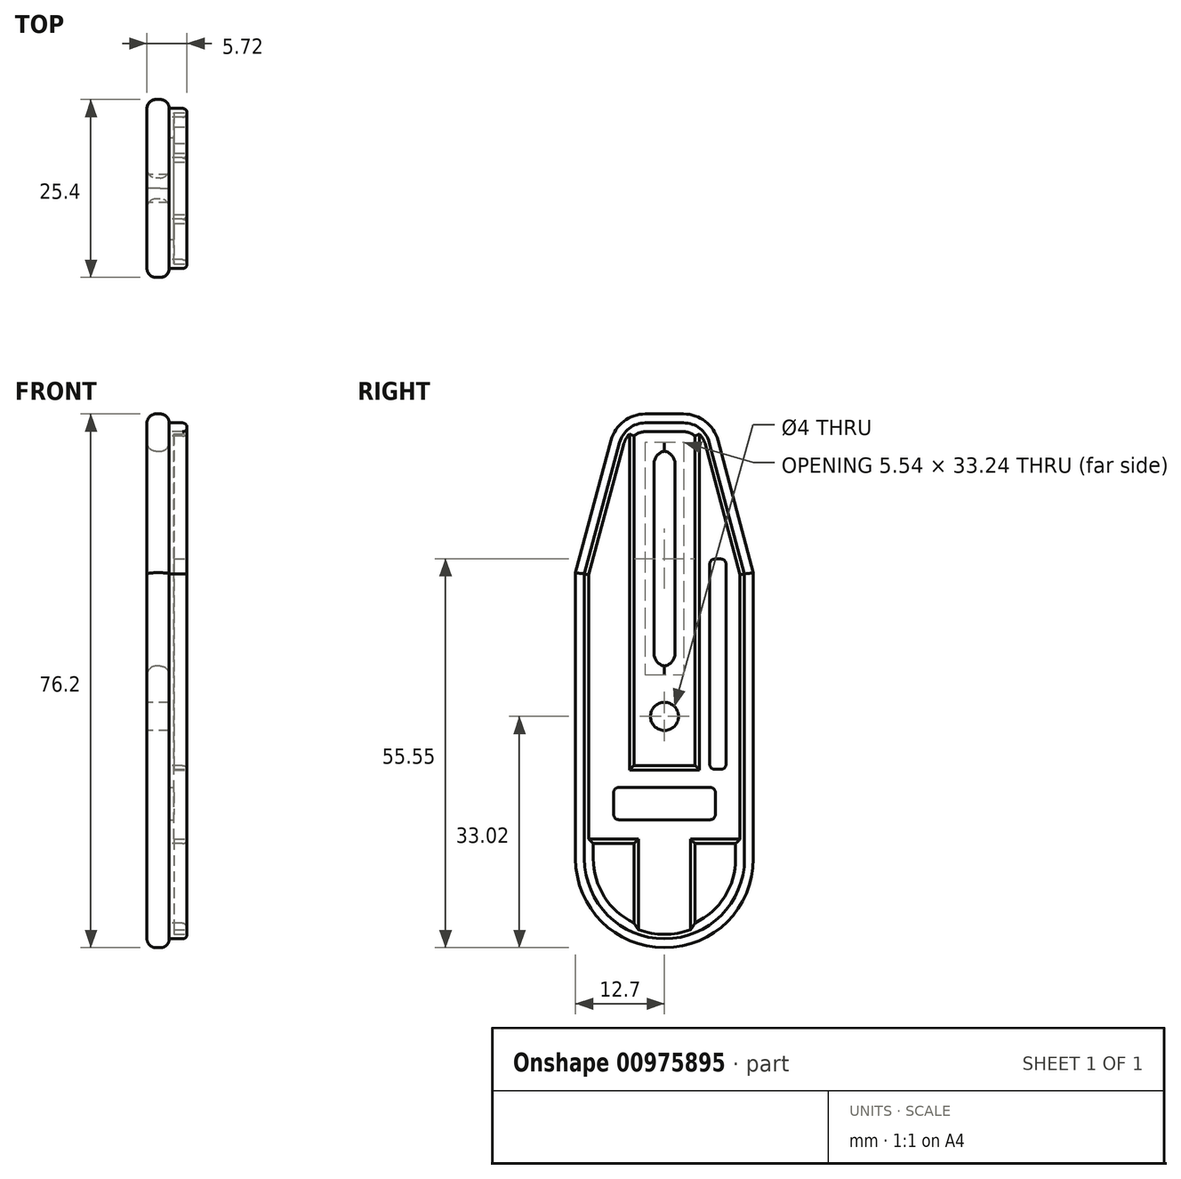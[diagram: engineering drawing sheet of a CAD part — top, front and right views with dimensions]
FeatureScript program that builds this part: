
annotation { "Feature Type Name" : "Feature", "Feature Type Description" : "" }
export const myFeature = defineFeature(function(context is Context, id is Id, definition is map)
    precondition{}
    {
        {
            var Q0;
            Q0=qCreatedBy(makeId("Right.planeOp"),FACE);
            var sketch = newSketch(context, id + "F0", { "sketchPlane" : qUnion([Q0])});
            skLineSegment(sketch, "E0", {"start": v(0, 0) * mm, "end": v(0, -40.83) * mm});
            skLineSegment(sketch, "E1", {"start": v(0, -40.83) * mm, "end": v(25.4, -40.83) * mm});
            skLineSegment(sketch, "E2", {"start": v(25.4, -40.83) * mm, "end": v(25.4, 0) * mm});
            skLineSegment(sketch, "E3", {"start": v(0, 0) * mm, "end": v(6.07, 22.67) * mm});
            skLineSegment(sketch, "E4", {"start": v(6.07, 22.67) * mm, "end": v(19.33, 22.67) * mm});
            skLineSegment(sketch, "E5", {"start": v(19.33, 22.67) * mm, "end": v(25.4, 0) * mm});
            skLineSegment(sketch, "E6.bottom", {"start": v(11.2, 17.39) * mm, "end": v(14.2, 17.39) * mm});
            skLineSegment(sketch, "E6.top", {"start": v(11.2, -13.35) * mm, "end": v(14.2, -13.35) * mm});
            skLineSegment(sketch, "E6.left", {"start": v(11.2, 17.39) * mm, "end": v(11.2, -13.35) * mm});
            skLineSegment(sketch, "E6.right", {"start": v(14.2, 17.39) * mm, "end": v(14.2, -13.35) * mm});
            skCircle(sketch, "E7", {"center": v(12.7, -20.5) * mm, "radius": 2 * mm});
            skPoint(sketch, "E7.centerSnap0", {"position": v(12.7, -13.35) * mm});
            skArc(sketch, "E8", {"start": v(0, -40.83) * mm, "mid": v(12.7, -53.53) * mm, "end": v(25.4, -40.83) * mm});
            skLineSegment(sketch, "E9", {"start": v(12.7, -53.53) * mm, "end": v(28.38, -53.53) * mm, "construction": true});
            skLineSegment(sketch, "E10", {"start": v(12.7, -20.5) * mm, "end": v(25.4, -20.5) * mm, "construction": true});
            skLineSegment(sketch, "E11", {"start": v(12.7, -20.5) * mm, "end": v(0, -20.5) * mm, "construction": true});
            skSolve(sketch);
        }
        {
            var Q0;
            Q0=makeQuery(id+"F0.imprint","IMPRINT",FACE,{"disambiguationData":[TD([[makeQuery(id+"F0.imprint","IMPRINT",EDGE,{"derivedFrom":sQuery(id+"F0.wireOp",EDGE,"E0")}),1.0]])]});
            extrude(context, id + "F1", {"entities" : qUnion([Q0]), "depth" : 3.17 * mm, "offsetDistance" : 25.4 * mm});
        }
        {
            var Q0;
            Q0=makeQuery(id+"F0.imprint","IMPRINT",FACE,{"disambiguationData":[TD([[makeQuery(id+"F0.imprint","IMPRINT",EDGE,{"derivedFrom":sQuery(id+"F0.wireOp",EDGE,"E1")}),-1.0]])]});
            extrude(context, id + "F2", {"entities" : qUnion([Q0]), "operationType" : NewBodyOperationType.ADD, "depth" : 3.17 * mm, "offsetDistance" : 25.4 * mm});
        }
        {
            var Q0;
            Q0=makeQuery(id+"F1.opExtrude","SWEPT_EDGE",EDGE,{"disambiguationData":[OSD([sQuery(id+"F0.wireOp",EDGE,"E3"),sQuery(id+"F0.wireOp",EDGE,"E4")])]});
            var Q1;
            Q1=makeQuery(id+"F1.opExtrude","SWEPT_EDGE",EDGE,{"disambiguationData":[OSD([sQuery(id+"F0.wireOp",EDGE,"E4"),sQuery(id+"F0.wireOp",EDGE,"E5")])]});
            fillet(context, id + "F3", {"entities" : qUnion([Q0, Q1]), "radius" : 5.08 * mm, "tangentPropagation" : true, "allowEdgeOverflow" : false});
        }
        {
            var Q0;
            Q0=makeQuery(id+"F1.opExtrude","SWEPT_EDGE",EDGE,{"disambiguationData":[OSD([sQuery(id+"F0.wireOp",EDGE,"E6.bottom"),sQuery(id+"F0.wireOp",EDGE,"E6.right")])]});
            var Q1;
            Q1=makeQuery(id+"F1.opExtrude","SWEPT_EDGE",EDGE,{"disambiguationData":[OSD([sQuery(id+"F0.wireOp",EDGE,"E6.bottom"),sQuery(id+"F0.wireOp",EDGE,"E6.left")])]});
            var Q2;
            Q2=makeQuery(id+"F1.opExtrude","SWEPT_EDGE",EDGE,{"disambiguationData":[OSD([sQuery(id+"F0.wireOp",EDGE,"E6.top"),sQuery(id+"F0.wireOp",EDGE,"E6.right")])]});
            var Q3;
            Q3=makeQuery(id+"F1.opExtrude","SWEPT_EDGE",EDGE,{"disambiguationData":[OSD([sQuery(id+"F0.wireOp",EDGE,"E6.top"),sQuery(id+"F0.wireOp",EDGE,"E6.left")])]});
            fillet(context, id + "F4", {"entities" : qUnion([Q0, Q1, Q2, Q3]), "radius" : 1.84 * mm, "tangentPropagation" : true, "allowEdgeOverflow" : false});
        }
        {
            var Q0;
            Q0=makeQuery(id+"F1.opExtrude","CAP_EDGE",EDGE,{"disambiguationData":[OSD([sQuery(id+"F0.wireOp",EDGE,"E4")])],"isStart":false});
            var Q1;
            Q1=makeQuery(id+"F2.opExtrude","CAP_EDGE",EDGE,{"disambiguationData":[OSD([sQuery(id+"F0.wireOp",EDGE,"E8")])],"isStart":false});
            var Q2;
            Q2=makeQuery(id+"F1.opExtrude","CAP_EDGE",EDGE,{"disambiguationData":[OSD([sQuery(id+"F0.wireOp",EDGE,"E4")])],"isStart":true});
            var Q3;
            Q3=makeQuery(id+"F2.opExtrude","CAP_EDGE",EDGE,{"disambiguationData":[OSD([sQuery(id+"F0.wireOp",EDGE,"E8")])],"isStart":true});
            fillet(context, id + "F5", {"entities" : qUnion([Q0, Q1, Q2, Q3]), "radius" : 1.27 * mm, "tangentPropagation" : true, "allowEdgeOverflow" : false});
        }
        {
            var Q0;
            {var subQ0=sQuery(id+"F0.wireOp",EDGE,"E1");var subQ1=sQuery(id+"F0.wireOp",EDGE,"E6.right");var subQ2=sQuery(id+"F0.wireOp",EDGE,"E6.top");Q0=makeQuery(id+"F4.opFillet","BLEND_EDGE",EDGE,{"blendedFrom":[makeQuery(id+"F1.opExtrude","SWEPT_EDGE",EDGE,{"disambiguationData":[OSD([subQ2,subQ1])]}),makeQuery(id+"F2.boolean.opBoolean","MERGE",FACE,{"derivedFrom":[makeQuery(id+"F1.opExtrude","CAP_FACE",FACE,{"disambiguationData":[OSD([sQuery(id+"F0.wireOp",EDGE,"E0"),subQ0,sQuery(id+"F0.wireOp",EDGE,"E2"),sQuery(id+"F0.wireOp",EDGE,"E3"),sQuery(id+"F0.wireOp",EDGE,"E4"),sQuery(id+"F0.wireOp",EDGE,"E5"),sQuery(id+"F0.wireOp",EDGE,"E6.bottom"),subQ2,sQuery(id+"F0.wireOp",EDGE,"E6.left"),subQ1,sQuery(id+"F0.wireOp",EDGE,"E7")])],"isStart":false}),makeQuery(id+"F2.opExtrude","CAP_FACE",FACE,{"disambiguationData":[OSD([subQ0,sQuery(id+"F0.wireOp",EDGE,"E8")])],"isStart":false})]})],"blendedInto":[makeQuery(id+"F2.boolean.opBoolean","MERGE",FACE,{"derivedFrom":[makeQuery(id+"F1.opExtrude","CAP_FACE",FACE,{"disambiguationData":[OSD([sQuery(id+"F0.wireOp",EDGE,"E0"),subQ0,sQuery(id+"F0.wireOp",EDGE,"E2"),sQuery(id+"F0.wireOp",EDGE,"E3"),sQuery(id+"F0.wireOp",EDGE,"E4"),sQuery(id+"F0.wireOp",EDGE,"E5"),sQuery(id+"F0.wireOp",EDGE,"E6.bottom"),subQ2,sQuery(id+"F0.wireOp",EDGE,"E6.left"),subQ1,sQuery(id+"F0.wireOp",EDGE,"E7")])],"isStart":false}),makeQuery(id+"F2.opExtrude","CAP_FACE",FACE,{"disambiguationData":[OSD([subQ0,sQuery(id+"F0.wireOp",EDGE,"E8")])],"isStart":false})]})]});}
            var Q1;
            {var subQ0=sQuery(id+"F0.wireOp",EDGE,"E1");var subQ1=sQuery(id+"F0.wireOp",EDGE,"E6.left");var subQ2=sQuery(id+"F0.wireOp",EDGE,"E6.top");Q1=makeQuery(id+"F4.opFillet","BLEND_EDGE",EDGE,{"blendedFrom":[makeQuery(id+"F1.opExtrude","SWEPT_EDGE",EDGE,{"disambiguationData":[OSD([subQ2,subQ1])]}),makeQuery(id+"F2.boolean.opBoolean","MERGE",FACE,{"derivedFrom":[makeQuery(id+"F1.opExtrude","CAP_FACE",FACE,{"disambiguationData":[OSD([sQuery(id+"F0.wireOp",EDGE,"E0"),subQ0,sQuery(id+"F0.wireOp",EDGE,"E2"),sQuery(id+"F0.wireOp",EDGE,"E3"),sQuery(id+"F0.wireOp",EDGE,"E4"),sQuery(id+"F0.wireOp",EDGE,"E5"),sQuery(id+"F0.wireOp",EDGE,"E6.bottom"),subQ2,subQ1,sQuery(id+"F0.wireOp",EDGE,"E6.right"),sQuery(id+"F0.wireOp",EDGE,"E7")])],"isStart":false}),makeQuery(id+"F2.opExtrude","CAP_FACE",FACE,{"disambiguationData":[OSD([subQ0,sQuery(id+"F0.wireOp",EDGE,"E8")])],"isStart":false})]})],"blendedInto":[makeQuery(id+"F2.boolean.opBoolean","MERGE",FACE,{"derivedFrom":[makeQuery(id+"F1.opExtrude","CAP_FACE",FACE,{"disambiguationData":[OSD([sQuery(id+"F0.wireOp",EDGE,"E0"),subQ0,sQuery(id+"F0.wireOp",EDGE,"E2"),sQuery(id+"F0.wireOp",EDGE,"E3"),sQuery(id+"F0.wireOp",EDGE,"E4"),sQuery(id+"F0.wireOp",EDGE,"E5"),sQuery(id+"F0.wireOp",EDGE,"E6.bottom"),subQ2,subQ1,sQuery(id+"F0.wireOp",EDGE,"E6.right"),sQuery(id+"F0.wireOp",EDGE,"E7")])],"isStart":false}),makeQuery(id+"F2.opExtrude","CAP_FACE",FACE,{"disambiguationData":[OSD([subQ0,sQuery(id+"F0.wireOp",EDGE,"E8")])],"isStart":false})]})]});}
            var Q2;
            Q2=makeQuery(id+"F1.opExtrude","CAP_EDGE",EDGE,{"disambiguationData":[OSD([sQuery(id+"F0.wireOp",EDGE,"E6.left")])],"isStart":true});
            var Q3;
            {var subQ0=sQuery(id+"F0.wireOp",EDGE,"E1");var subQ1=sQuery(id+"F0.wireOp",EDGE,"E6.left");var subQ2=sQuery(id+"F0.wireOp",EDGE,"E6.top");Q3=makeQuery(id+"F4.opFillet","BLEND_EDGE",EDGE,{"blendedFrom":[makeQuery(id+"F1.opExtrude","SWEPT_EDGE",EDGE,{"disambiguationData":[OSD([subQ2,subQ1])]}),makeQuery(id+"F2.boolean.opBoolean","MERGE",FACE,{"derivedFrom":[makeQuery(id+"F1.opExtrude","CAP_FACE",FACE,{"disambiguationData":[OSD([sQuery(id+"F0.wireOp",EDGE,"E0"),subQ0,sQuery(id+"F0.wireOp",EDGE,"E2"),sQuery(id+"F0.wireOp",EDGE,"E3"),sQuery(id+"F0.wireOp",EDGE,"E4"),sQuery(id+"F0.wireOp",EDGE,"E5"),sQuery(id+"F0.wireOp",EDGE,"E6.bottom"),subQ2,subQ1,sQuery(id+"F0.wireOp",EDGE,"E6.right"),sQuery(id+"F0.wireOp",EDGE,"E7")])],"isStart":true}),makeQuery(id+"F2.opExtrude","CAP_FACE",FACE,{"disambiguationData":[OSD([subQ0,sQuery(id+"F0.wireOp",EDGE,"E8")])],"isStart":true})]})],"blendedInto":[makeQuery(id+"F2.boolean.opBoolean","MERGE",FACE,{"derivedFrom":[makeQuery(id+"F1.opExtrude","CAP_FACE",FACE,{"disambiguationData":[OSD([sQuery(id+"F0.wireOp",EDGE,"E0"),subQ0,sQuery(id+"F0.wireOp",EDGE,"E2"),sQuery(id+"F0.wireOp",EDGE,"E3"),sQuery(id+"F0.wireOp",EDGE,"E4"),sQuery(id+"F0.wireOp",EDGE,"E5"),sQuery(id+"F0.wireOp",EDGE,"E6.bottom"),subQ2,subQ1,sQuery(id+"F0.wireOp",EDGE,"E6.right"),sQuery(id+"F0.wireOp",EDGE,"E7")])],"isStart":true}),makeQuery(id+"F2.opExtrude","CAP_FACE",FACE,{"disambiguationData":[OSD([subQ0,sQuery(id+"F0.wireOp",EDGE,"E8")])],"isStart":true})]})]});}
            var Q4;
            {var subQ0=sQuery(id+"F0.wireOp",EDGE,"E1");var subQ1=sQuery(id+"F0.wireOp",EDGE,"E6.right");var subQ2=sQuery(id+"F0.wireOp",EDGE,"E6.top");Q4=makeQuery(id+"F4.opFillet","BLEND_EDGE",EDGE,{"blendedFrom":[makeQuery(id+"F1.opExtrude","SWEPT_EDGE",EDGE,{"disambiguationData":[OSD([subQ2,subQ1])]}),makeQuery(id+"F2.boolean.opBoolean","MERGE",FACE,{"derivedFrom":[makeQuery(id+"F1.opExtrude","CAP_FACE",FACE,{"disambiguationData":[OSD([sQuery(id+"F0.wireOp",EDGE,"E0"),subQ0,sQuery(id+"F0.wireOp",EDGE,"E2"),sQuery(id+"F0.wireOp",EDGE,"E3"),sQuery(id+"F0.wireOp",EDGE,"E4"),sQuery(id+"F0.wireOp",EDGE,"E5"),sQuery(id+"F0.wireOp",EDGE,"E6.bottom"),subQ2,sQuery(id+"F0.wireOp",EDGE,"E6.left"),subQ1,sQuery(id+"F0.wireOp",EDGE,"E7")])],"isStart":true}),makeQuery(id+"F2.opExtrude","CAP_FACE",FACE,{"disambiguationData":[OSD([subQ0,sQuery(id+"F0.wireOp",EDGE,"E8")])],"isStart":true})]})],"blendedInto":[makeQuery(id+"F2.boolean.opBoolean","MERGE",FACE,{"derivedFrom":[makeQuery(id+"F1.opExtrude","CAP_FACE",FACE,{"disambiguationData":[OSD([sQuery(id+"F0.wireOp",EDGE,"E0"),subQ0,sQuery(id+"F0.wireOp",EDGE,"E2"),sQuery(id+"F0.wireOp",EDGE,"E3"),sQuery(id+"F0.wireOp",EDGE,"E4"),sQuery(id+"F0.wireOp",EDGE,"E5"),sQuery(id+"F0.wireOp",EDGE,"E6.bottom"),subQ2,sQuery(id+"F0.wireOp",EDGE,"E6.left"),subQ1,sQuery(id+"F0.wireOp",EDGE,"E7")])],"isStart":true}),makeQuery(id+"F2.opExtrude","CAP_FACE",FACE,{"disambiguationData":[OSD([subQ0,sQuery(id+"F0.wireOp",EDGE,"E8")])],"isStart":true})]})]});}
            var Q5;
            Q5=makeQuery(id+"F1.opExtrude","CAP_EDGE",EDGE,{"disambiguationData":[OSD([sQuery(id+"F0.wireOp",EDGE,"E6.right")])],"isStart":true});
            fillet(context, id + "F6", {"entities" : qUnion([Q0, Q1, Q2, Q3, Q4, Q5]), "radius" : 1.27 * mm, "tangentPropagation" : true, "allowEdgeOverflow" : false});
        }
        {
            var Q0;
            {var subQ0=sQuery(id+"F0.wireOp",EDGE,"E1");Q0=makeQuery(id+"F2.boolean.opBoolean","MERGE",FACE,{"derivedFrom":[makeQuery(id+"F1.opExtrude","CAP_FACE",FACE,{"disambiguationData":[OSD([sQuery(id+"F0.wireOp",EDGE,"E0"),subQ0,sQuery(id+"F0.wireOp",EDGE,"E2"),sQuery(id+"F0.wireOp",EDGE,"E3"),sQuery(id+"F0.wireOp",EDGE,"E4"),sQuery(id+"F0.wireOp",EDGE,"E5"),sQuery(id+"F0.wireOp",EDGE,"E6.bottom"),sQuery(id+"F0.wireOp",EDGE,"E6.top"),sQuery(id+"F0.wireOp",EDGE,"E6.left"),sQuery(id+"F0.wireOp",EDGE,"E6.right"),sQuery(id+"F0.wireOp",EDGE,"E7")])],"isStart":false}),makeQuery(id+"F2.opExtrude","CAP_FACE",FACE,{"disambiguationData":[OSD([subQ0,sQuery(id+"F0.wireOp",EDGE,"E8")])],"isStart":false})]});}
            var sketch = newSketch(context, id + "F7", { "sketchPlane" : qUnion([Q0])});
            skLineSegment(sketch, "E12.0", {"start": v(22.86, -0.33) * mm, "end": v(17.89, 18.25) * mm});
            skLineSegment(sketch, "E12.1", {"start": v(22.86, -40.83) * mm, "end": v(22.86, -0.33) * mm});
            skArc(sketch, "E12.2", {"start": v(17.89, 18.25) * mm, "mid": v(16.98, 19.6) * mm, "end": v(15.43, 20.13) * mm});
            skArc(sketch, "E12.3", {"start": v(2.54, -40.83) * mm, "mid": v(12.7, -50.99) * mm, "end": v(22.86, -40.83) * mm});
            skLineSegment(sketch, "E12.4", {"start": v(15.43, 20.13) * mm, "end": v(9.97, 20.13) * mm});
            skArc(sketch, "E12.5", {"start": v(9.97, 20.13) * mm, "mid": v(8.42, 19.6) * mm, "end": v(7.51, 18.25) * mm});
            skLineSegment(sketch, "E12.6", {"start": v(7.51, 18.25) * mm, "end": v(2.54, -0.33) * mm});
            skLineSegment(sketch, "E12.7", {"start": v(2.54, -0.33) * mm, "end": v(2.54, -40.83) * mm});
            skLineSegment(sketch, "E13.bottom", {"start": v(2.54, -27.5) * mm, "end": v(22.86, -27.5) * mm});
            skLineSegment(sketch, "E13.top", {"start": v(2.54, -38.67) * mm, "end": v(22.86, -38.67) * mm});
            skLineSegment(sketch, "E13.left", {"start": v(2.54, -27.5) * mm, "end": v(2.54, -38.67) * mm});
            skLineSegment(sketch, "E13.right", {"start": v(22.86, -27.5) * mm, "end": v(22.86, -38.67) * mm});
            skLineSegment(sketch, "E14", {"start": v(8.33, 21.3) * mm, "end": v(8.33, -27.5) * mm});
            skLineSegment(sketch, "E15", {"start": v(12.7, -20.5) * mm, "end": v(12.7, -50.99) * mm, "construction": true});
            skLineSegment(sketch, "E16.MirrorCS", {"start": v(17.07, 21.3) * mm, "end": v(17.07, -27.5) * mm});
            skLineSegment(sketch, "E17", {"start": v(2.54, -0.33) * mm, "end": v(2.54, -27.5) * mm});
            skLineSegment(sketch, "E18", {"start": v(8.33, -27.5) * mm, "end": v(17.07, -27.5) * mm});
            skLineSegment(sketch, "E19", {"start": v(22.86, -0.33) * mm, "end": v(22.86, -27.5) * mm});
            skLineSegment(sketch, "E20", {"start": v(8.33, -38.67) * mm, "end": v(8.33, -50) * mm});
            skLineSegment(sketch, "E21", {"start": v(17.07, -38.67) * mm, "end": v(17.07, -50) * mm});
            skSolve(sketch);
        }
        {
            var Q0;
            {var subQ0=sQuery(id+"F7.wireOp",EDGE,"CffNSvqF-yRKR-SQpj-RTyX-08ctVP1XR6EA");Q0=makeQuery(id+"F7.imprint","IMPRINT",FACE,{"disambiguationData":[TD([[makeQuery(id+"F7.imprint","IMPRINT",EDGE,{"derivedFrom":subQ0}),-1.0]])]});}
            var Q1;
            {var subQ0=sQuery(id+"F7.wireOp",EDGE,"dPliOB4x-Hba5-WOCV-d6CY-ONObMFQEq9AN");Q1=makeQuery(id+"F7.imprint","IMPRINT",FACE,{"disambiguationData":[TD([[makeQuery(id+"F7.imprint","IMPRINT",EDGE,{"derivedFrom":subQ0}),1.0]])]});}
            var Q2;
            {var subQ12=sQuery(id+"F7.wireOp",EDGE,"E12.0");Q2=makeQuery(id+"F7.imprint","IMPRINT",FACE,{"disambiguationData":[TD([[makeQuery(id+"F7.imprint","IMPRINT",EDGE,{"derivedFrom":subQ12}),-1.0]])]});}
            var Q3;
            {var subQ0=sQuery(id+"F7.wireOp",EDGE,"XRLydO9e-xz2z-3hUB-Hhj4-1X3KUHKsZLNA");Q3=makeQuery(id+"F7.imprint","IMPRINT",FACE,{"disambiguationData":[TD([[makeQuery(id+"F7.imprint","IMPRINT",EDGE,{"derivedFrom":subQ0}),-1.0]])]});}
            var Q4;
            {var subQ11=sQuery(id+"F7.wireOp",EDGE,"E12.4");Q4=makeQuery(id+"F7.imprint","IMPRINT",FACE,{"disambiguationData":[TD([[makeQuery(id+"F7.imprint","IMPRINT",EDGE,{"derivedFrom":subQ11}),-1.0]])]});}
            extrude(context, id + "F8", {"entities" : qUnion([Q0, Q1, Q2, Q3, Q4]), "operationType" : NewBodyOperationType.ADD, "depth" : 2.54 * mm, "offsetDistance" : 25.4 * mm});
        }
        {
            var Q0;
            {var subQ2=sQuery(id+"F7.wireOp",EDGE,"E14");Q0=makeQuery(id+"F7.imprint","IMPRINT",FACE,{"disambiguationData":[TD([[makeQuery(id+"F7.imprint","IMPRINT",EDGE,{"derivedFrom":subQ2}),-1.0]])]});}
            var Q1;
            {var subQ2=sQuery(id+"F7.wireOp",EDGE,"E16.MirrorCS");Q1=makeQuery(id+"F7.imprint","IMPRINT",FACE,{"disambiguationData":[TD([[makeQuery(id+"F7.imprint","IMPRINT",EDGE,{"derivedFrom":subQ2}),1.0]])]});}
            var Q2;
            Q2=makeQuery(id+"F7.imprint","IMPRINT",FACE,{"disambiguationData":[TD([[makeQuery(id+"F7.imprint","IMPRINT",EDGE,{"derivedFrom":sQuery(id+"F7.wireOp",EDGE,"E13.top")}),1.0]])]});
            var Q3;
            {var subQ0=sQuery(id+"F7.wireOp",EDGE,"E20");Q3=makeQuery(id+"F7.imprint","IMPRINT",FACE,{"disambiguationData":[TD([[makeQuery(id+"F7.imprint","IMPRINT",EDGE,{"derivedFrom":subQ0}),1.0]])]});}
            extrude(context, id + "F9", {"entities" : qUnion([Q0, Q1, Q2, Q3]), "operationType" : NewBodyOperationType.ADD, "depth" : 2.54 * mm, "offsetDistance" : 25.4 * mm});
        }
        {
            var Q0;
            {var subQ0=sQuery(id+"F7.wireOp",EDGE,"E13.right");var subQ1=sQuery(id+"F7.wireOp",EDGE,"E13.left");var subQ2=sQuery(id+"F7.wireOp",EDGE,"E12.6");var subQ3=sQuery(id+"F7.wireOp",EDGE,"E12.3");var subQ4=sQuery(id+"F7.wireOp",EDGE,"E12.0");Q0=makeQuery(id+"F9.boolean.opBoolean","MERGE",FACE,{"derivedFrom":[makeQuery(id+"F8.opExtrude","CAP_FACE",FACE,{"disambiguationData":[OSD([sQuery(id+"F0.wireOp",EDGE,"E0"),sQuery(id+"F0.wireOp",EDGE,"E1"),sQuery(id+"F0.wireOp",EDGE,"E2"),sQuery(id+"F0.wireOp",EDGE,"E3"),sQuery(id+"F0.wireOp",EDGE,"E4"),sQuery(id+"F0.wireOp",EDGE,"E5"),sQuery(id+"F0.wireOp",EDGE,"E6.bottom"),sQuery(id+"F0.wireOp",EDGE,"E6.top"),sQuery(id+"F0.wireOp",EDGE,"E6.left"),sQuery(id+"F0.wireOp",EDGE,"E6.right"),sQuery(id+"F0.wireOp",EDGE,"E7"),sQuery(id+"F0.wireOp",EDGE,"E8"),subQ4,sQuery(id+"F7.wireOp",EDGE,"E12.1"),sQuery(id+"F7.wireOp",EDGE,"E12.2"),subQ3,sQuery(id+"F7.wireOp",EDGE,"E12.4"),sQuery(id+"F7.wireOp",EDGE,"E12.5"),subQ2,sQuery(id+"F7.wireOp",EDGE,"E12.7"),subQ1,subQ0])],"isStart":false}),makeQuery(id+"F9.opExtrude","CAP_FACE",FACE,{"disambiguationData":[OSD([subQ4,subQ3,subQ2,sQuery(id+"F7.wireOp",EDGE,"E13.bottom"),sQuery(id+"F7.wireOp",EDGE,"E13.top"),subQ1,subQ0,sQuery(id+"F7.wireOp",EDGE,"E14"),sQuery(id+"F7.wireOp",EDGE,"E16.MirrorCS"),sQuery(id+"F7.wireOp",EDGE,"E17"),sQuery(id+"F7.wireOp",EDGE,"E18"),sQuery(id+"F7.wireOp",EDGE,"E19"),sQuery(id+"F7.wireOp",EDGE,"E20"),sQuery(id+"F7.wireOp",EDGE,"E21")])],"isStart":false})]});}
            fillet(context, id + "F10", {"entities" : qUnion([Q0]), "tangentPropagation" : true, "radius" : 0.64 * mm, "defaultsChanged" : false, "vertexSettings" : [], "allowEdgeOverflow" : false});
        }
        {
            var Q0;
            {var subQ0=sQuery(id+"F7.wireOp",EDGE,"E19");var subQ1=sQuery(id+"F7.wireOp",EDGE,"E17");var subQ2=sQuery(id+"F7.wireOp",EDGE,"E13.right");var subQ3=sQuery(id+"F7.wireOp",EDGE,"E13.left");var subQ4=sQuery(id+"F7.wireOp",EDGE,"E12.6");var subQ5=sQuery(id+"F7.wireOp",EDGE,"E12.5");var subQ6=sQuery(id+"F7.wireOp",EDGE,"E12.3");var subQ7=sQuery(id+"F7.wireOp",EDGE,"E12.2");var subQ8=sQuery(id+"F7.wireOp",EDGE,"E12.0");Q0=makeQuery(id+"F9.boolean.opBoolean","MERGE",FACE,{"derivedFrom":[makeQuery(id+"F8.opExtrude","CAP_FACE",FACE,{"disambiguationData":[OSD([sQuery(id+"F0.wireOp",EDGE,"E0"),sQuery(id+"F0.wireOp",EDGE,"E1"),sQuery(id+"F0.wireOp",EDGE,"E2"),sQuery(id+"F0.wireOp",EDGE,"E3"),sQuery(id+"F0.wireOp",EDGE,"E4"),sQuery(id+"F0.wireOp",EDGE,"E5"),sQuery(id+"F0.wireOp",EDGE,"E6.bottom"),sQuery(id+"F0.wireOp",EDGE,"E6.top"),sQuery(id+"F0.wireOp",EDGE,"E6.left"),sQuery(id+"F0.wireOp",EDGE,"E6.right"),sQuery(id+"F0.wireOp",EDGE,"E7"),sQuery(id+"F0.wireOp",EDGE,"E8"),subQ8,sQuery(id+"F7.wireOp",EDGE,"E12.1"),subQ7,subQ6,sQuery(id+"F7.wireOp",EDGE,"E12.4"),subQ5,subQ4,sQuery(id+"F7.wireOp",EDGE,"E12.7"),subQ3,subQ2,subQ1,subQ0])],"isStart":false}),makeQuery(id+"F9.opExtrude","CAP_FACE",FACE,{"disambiguationData":[OSD([subQ8,subQ7,subQ6,subQ5,subQ4,sQuery(id+"F7.wireOp",EDGE,"E13.top"),subQ3,subQ2,sQuery(id+"F7.wireOp",EDGE,"E14"),sQuery(id+"F7.wireOp",EDGE,"E16.MirrorCS"),subQ1,sQuery(id+"F7.wireOp",EDGE,"E18"),subQ0,sQuery(id+"F7.wireOp",EDGE,"E20"),sQuery(id+"F7.wireOp",EDGE,"E21")])],"isStart":false})]});}
            var sketch = newSketch(context, id + "F11", { "sketchPlane" : qUnion([Q0])});
            skPoint(sketch, "E22.firstSnap0", {"position": v(5.43, -38.03) * mm});
            skPoint(sketch, "E22.oppositeSnap0", {"position": v(19.97, -38.03) * mm});
            skLineSegment(sketch, "E22.bottom", {"start": v(6.16, -30.65) * mm, "end": v(19.24, -30.65) * mm});
            skLineSegment(sketch, "E22.top", {"start": v(6.16, -35.25) * mm, "end": v(19.24, -35.25) * mm});
            skLineSegment(sketch, "E22.left", {"start": v(5.43, -31.37) * mm, "end": v(5.43, -34.52) * mm});
            skLineSegment(sketch, "E22.right", {"start": v(19.97, -31.37) * mm, "end": v(19.97, -34.52) * mm});
            skPoint(sketch, "E23.visualSharp", {"position": v(5.43, -30.65) * mm});
            skArc(sketch, "E23.filletArc", {"start": v(6.16, -30.65) * mm, "mid": v(5.65, -30.86) * mm, "end": v(5.43, -31.37) * mm});
            skPoint(sketch, "E24.visualSharp", {"position": v(19.97, -30.65) * mm});
            skArc(sketch, "E24.filletArc", {"start": v(19.97, -31.37) * mm, "mid": v(19.75, -30.86) * mm, "end": v(19.24, -30.65) * mm});
            skPoint(sketch, "E25.visualSharp", {"position": v(19.97, -35.25) * mm});
            skArc(sketch, "E25.filletArc", {"start": v(19.24, -35.25) * mm, "mid": v(19.75, -35.04) * mm, "end": v(19.97, -34.52) * mm});
            skPoint(sketch, "E26.visualSharp", {"position": v(5.43, -35.25) * mm});
            skArc(sketch, "E26.filletArc", {"start": v(5.43, -34.52) * mm, "mid": v(5.65, -35.04) * mm, "end": v(6.16, -35.25) * mm});
            skLineSegment(sketch, "E27.bottom", {"start": v(4.54, 1.96) * mm, "end": v(5.43, 1.96) * mm});
            skLineSegment(sketch, "E27.top", {"start": v(4.54, -28.06) * mm, "end": v(5.43, -28.06) * mm});
            skLineSegment(sketch, "E27.left", {"start": v(3.81, 1.23) * mm, "end": v(3.81, -27.33) * mm});
            skLineSegment(sketch, "E27.right", {"start": v(6.16, 1.23) * mm, "end": v(6.16, -27.33) * mm});
            skLineSegment(sketch, "E28", {"start": v(12.66, 20.13) * mm, "end": v(12.66, -51.62) * mm, "construction": true});
            skPoint(sketch, "E29.visualSharp", {"position": v(3.81, 1.96) * mm});
            skArc(sketch, "E29.filletArc", {"start": v(4.54, 1.96) * mm, "mid": v(4.03, 1.75) * mm, "end": v(3.81, 1.23) * mm});
            skPoint(sketch, "E30.visualSharp", {"position": v(6.16, 1.96) * mm});
            skArc(sketch, "E30.filletArc", {"start": v(6.16, 1.23) * mm, "mid": v(5.95, 1.75) * mm, "end": v(5.43, 1.96) * mm});
            skPoint(sketch, "E31.visualSharp", {"position": v(3.81, -28.06) * mm});
            skArc(sketch, "E31.filletArc", {"start": v(3.81, -27.33) * mm, "mid": v(4.03, -27.85) * mm, "end": v(4.54, -28.06) * mm});
            skPoint(sketch, "E32.visualSharp", {"position": v(6.16, -28.06) * mm});
            skArc(sketch, "E32.filletArc", {"start": v(5.43, -28.06) * mm, "mid": v(5.95, -27.85) * mm, "end": v(6.16, -27.33) * mm});
            skArc(sketch, "E33.MirrorCS", {"start": v(19.15, 1.23) * mm, "mid": v(19.36, 1.75) * mm, "end": v(19.88, 1.96) * mm});
            skLineSegment(sketch, "E34.MirrorCS", {"start": v(20.77, 1.96) * mm, "end": v(19.88, 1.96) * mm});
            skPoint(sketch, "E35.MirrorP", {"position": v(19.15, 1.96) * mm});
            skLineSegment(sketch, "E36.MirrorCS", {"start": v(20.77, -28.06) * mm, "end": v(19.88, -28.06) * mm});
            skArc(sketch, "E37.MirrorCS", {"start": v(21.5, -27.33) * mm, "mid": v(21.29, -27.85) * mm, "end": v(20.77, -28.06) * mm});
            skArc(sketch, "E38.MirrorCS", {"start": v(19.88, -28.06) * mm, "mid": v(19.36, -27.85) * mm, "end": v(19.15, -27.33) * mm});
            skLineSegment(sketch, "E39.MirrorCS", {"start": v(19.15, 1.23) * mm, "end": v(19.15, -27.33) * mm});
            skLineSegment(sketch, "E40.MirrorCS", {"start": v(21.5, 1.23) * mm, "end": v(21.5, -27.33) * mm});
            skArc(sketch, "E41.MirrorCS", {"start": v(20.77, 1.96) * mm, "mid": v(21.29, 1.75) * mm, "end": v(21.5, 1.23) * mm});
            skSolve(sketch);
        }
        {
            var Q0;
            Q0=makeQuery(id+"F11.imprint","IMPRINT",FACE,{"disambiguationData":[TD([[makeQuery(id+"F11.imprint","IMPRINT",EDGE,{"derivedFrom":sQuery(id+"F11.wireOp",EDGE,"E22.bottom")}),-1.0]])]});
            extrude(context, id + "F12", {"entities" : qUnion([Q0]), "operationType" : NewBodyOperationType.REMOVE, "oppositeDirection" : true, "depth" : 2.54 * mm, "offsetDistance" : 25.4 * mm});
        }
        {
            var Q0;
            Q0=makeQuery(id+"F11.imprint","IMPRINT",FACE,{"disambiguationData":[TD([[makeQuery(id+"F11.imprint","IMPRINT",EDGE,{"derivedFrom":sQuery(id+"F11.wireOp",EDGE,"E27.bottom")}),-1.0]])]});
            var Q1;
            Q1=makeQuery(id+"F11.imprint","IMPRINT",FACE,{"disambiguationData":[TD([[makeQuery(id+"F11.imprint","IMPRINT",EDGE,{"derivedFrom":sQuery(id+"F11.wireOp",EDGE,"E37.MirrorCS")}),-1.0]])]});
            extrude(context, id + "F13", {"entities" : qUnion([Q0, Q1]), "operationType" : NewBodyOperationType.REMOVE, "oppositeDirection" : true, "depth" : 1.84 * mm, "offsetDistance" : 25.4 * mm});
        }
    });
